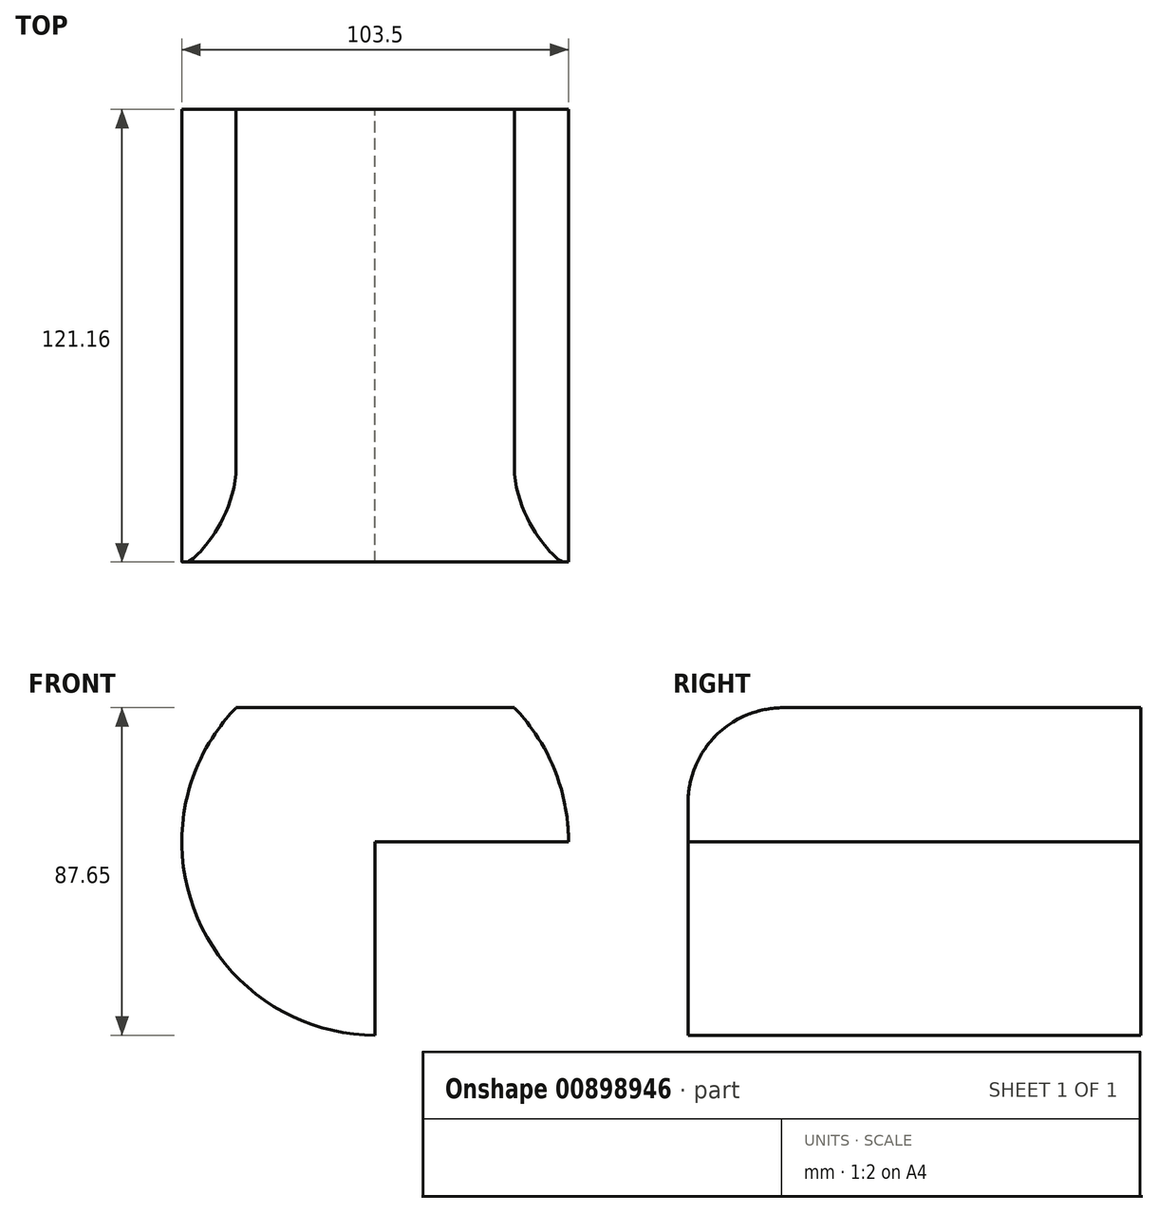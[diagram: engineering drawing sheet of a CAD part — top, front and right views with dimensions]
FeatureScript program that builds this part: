
annotation { "Feature Type Name" : "Feature", "Feature Type Description" : "" }
export const myFeature = defineFeature(function(context is Context, id is Id, definition is map)
    precondition{}
    {
        {
            var Q0;
            Q0=qCreatedBy(makeId("Front.planeOp"),FACE);
            var sketch = newSketch(context, id + "F0", { "sketchPlane" : qUnion([Q0])});
            skLineSegment(sketch, "E0.bottom", {"start": v(-79.68, 51.42) * mm, "end": v(87.5, 51.42) * mm});
            skLineSegment(sketch, "E0.top", {"start": v(-79.68, -65.24) * mm, "end": v(87.5, -65.24) * mm});
            skLineSegment(sketch, "E0.left", {"start": v(-79.68, 51.42) * mm, "end": v(-79.68, -65.24) * mm});
            skLineSegment(sketch, "E0.right", {"start": v(87.5, 51.42) * mm, "end": v(87.5, -65.24) * mm});
            skLineSegment(sketch, "E1.bottom", {"start": v(-12.73, 15.52) * mm, "end": v(87.5, 15.52) * mm});
            skLineSegment(sketch, "E1.top", {"start": v(-12.73, -40.61) * mm, "end": v(87.5, -40.61) * mm});
            skLineSegment(sketch, "E1.left", {"start": v(-12.73, 15.52) * mm, "end": v(-12.73, -40.61) * mm});
            skLineSegment(sketch, "E1.right", {"start": v(87.5, 15.52) * mm, "end": v(87.5, -40.61) * mm});
            skCircle(sketch, "E2", {"center": v(-12.73, 15.52) * mm, "radius": 51.75 * mm});
            skSolve(sketch);
        }
        {
            var Q0;
            {var subQ0=sQuery(id+"F0.wireOp",EDGE,"E2");var subQ1=sQuery(id+"F0.wireOp",EDGE,"E0.bottom");var subQ8=makeQuery(id+"F0.imprint","INTERSECT",VERTEX,{"disambiguationData":[OD(0.0)],"derivedFrom":[subQ1,subQ0]});Q0=makeQuery(id+"F0.imprint","IMPRINT",FACE,{"disambiguationData":[TD([[makeQuery(id+"F0.imprint","IMPRINT",EDGE,{"disambiguationData":[TD([[subQ8,-1.0]])],"derivedFrom":subQ1}),-1.0]])]});}
            extrude(context, id + "F1", {"entities" : qUnion([Q0]), "depth" : 121.16 * mm, "offsetDistance" : 25.4 * mm});
        }
        {
            var Q0;
            Q0=makeQuery(id+"F1.opExtrude","CAP_EDGE",EDGE,{"disambiguationData":[OSD([sQuery(id+"F0.wireOp",EDGE,"E0.bottom")])],"isStart":false});
            fillet(context, id + "F2", {"entities" : qUnion([Q0]), "radius" : 25.4 * mm, "tangentPropagation" : true, "allowEdgeOverflow" : false});
        }
    });
